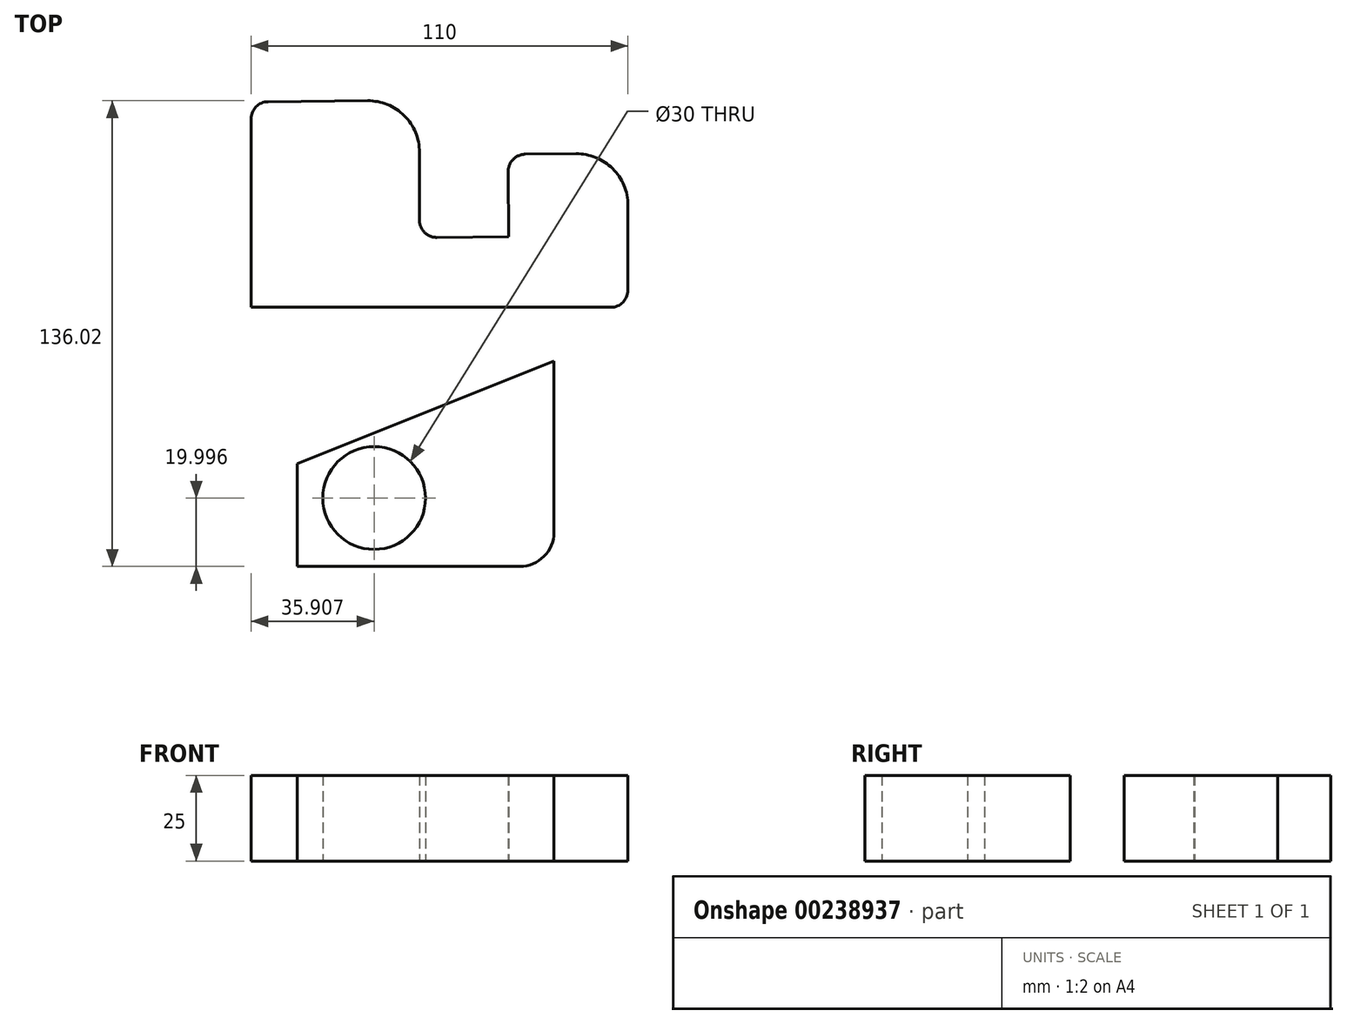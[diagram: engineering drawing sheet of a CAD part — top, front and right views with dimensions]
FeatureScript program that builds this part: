
annotation { "Feature Type Name" : "Feature", "Feature Type Description" : "" }
export const myFeature = defineFeature(function(context is Context, id is Id, definition is map)
    precondition{}
    {
        {
            var Q0;
            Q0=qCreatedBy(makeId("Top.planeOp"),FACE);
            var sketch = newSketch(context, id + "F0", { "sketchPlane" : qUnion([Q0])});
            skLineSegment(sketch, "E0", {"start": v(-56.6, 22.26) * mm, "end": v(48.4, 22.26) * mm});
            skLineSegment(sketch, "E1", {"start": v(53.4, 27.26) * mm, "end": v(53.4, 52.12) * mm});
            skLineSegment(sketch, "E2", {"start": v(23.4, 66.97) * mm, "end": v(38.25, 67.12) * mm});
            skLineSegment(sketch, "E3", {"start": v(18.45, 61.92) * mm, "end": v(18.64, 42.89) * mm});
            skLineSegment(sketch, "E4", {"start": v(18.64, 42.89) * mm, "end": v(-2.4, 42.68) * mm});
            skLineSegment(sketch, "E5", {"start": v(-56.6, 22.26) * mm, "end": v(-56.6, 77.31) * mm});
            skPoint(sketch, "E6.visualSharp", {"position": v(-56.6, 82.26) * mm});
            skArc(sketch, "E6.filletArc", {"start": v(-51.65, 82.31) * mm, "mid": v(-55.15, 80.83) * mm, "end": v(-56.6, 77.31) * mm});
            skPoint(sketch, "E7.visualSharp", {"position": v(-16.6, 42.55) * mm});
            skArc(sketch, "E7.filletArc", {"start": v(-7.44, 47.68) * mm, "mid": v(-5.96, 44.13) * mm, "end": v(-2.4, 42.68) * mm});
            skPoint(sketch, "E8.visualSharp", {"position": v(18.4, 66.92) * mm});
            skArc(sketch, "E8.filletArc", {"start": v(23.4, 66.97) * mm, "mid": v(19.88, 65.47) * mm, "end": v(18.45, 61.92) * mm});
            skPoint(sketch, "E9.visualSharp", {"position": v(53.4, 67.26) * mm});
            skArc(sketch, "E9.filletArc", {"start": v(53.4, 52.12) * mm, "mid": v(48.96, 62.78) * mm, "end": v(38.25, 67.12) * mm});
            skPoint(sketch, "E10.visualSharp", {"position": v(53.4, 22.26) * mm});
            skArc(sketch, "E10.filletArc", {"start": v(48.4, 22.26) * mm, "mid": v(51.94, 23.73) * mm, "end": v(53.4, 27.26) * mm});
            skLineSegment(sketch, "E11", {"start": v(-51.65, 82.31) * mm, "end": v(-22.59, 82.6) * mm});
            skLineSegment(sketch, "E12", {"start": v(-7.44, 47.68) * mm, "end": v(-7.44, 67.6) * mm});
            skPoint(sketch, "E13.visualSharp", {"position": v(-7.44, 82.74) * mm});
            skArc(sketch, "E13.filletArc", {"start": v(-7.44, 67.6) * mm, "mid": v(-11.89, 78.25) * mm, "end": v(-22.59, 82.6) * mm});
            skLineSegment(sketch, "E14", {"start": v(-43.2, -23.43) * mm, "end": v(-43.2, -53.43) * mm});
            skLineSegment(sketch, "E15", {"start": v(-43.2, -53.43) * mm, "end": v(21.8, -53.43) * mm});
            skLineSegment(sketch, "E16", {"start": v(31.8, -43.43) * mm, "end": v(31.8, 6.57) * mm});
            skLineSegment(sketch, "E17", {"start": v(-43.2, -23.43) * mm, "end": v(31.8, 6.57) * mm});
            skPoint(sketch, "E18.visualSharp", {"position": v(31.8, -53.43) * mm});
            skArc(sketch, "E18.filletArc", {"start": v(21.8, -53.43) * mm, "mid": v(28.88, -50.5) * mm, "end": v(31.8, -43.43) * mm});
            skCircle(sketch, "E19", {"center": v(-20.7, -33.43) * mm, "radius": 15 * mm});
            skSolve(sketch);
        }
        {
            var Q0;
            Q0 = qSketchRegion(id + "F0", true);
            extrude(context, id + "F1", {"entities" : qUnion([Q0]), "depth" : 25 * mm});
        }
    });
